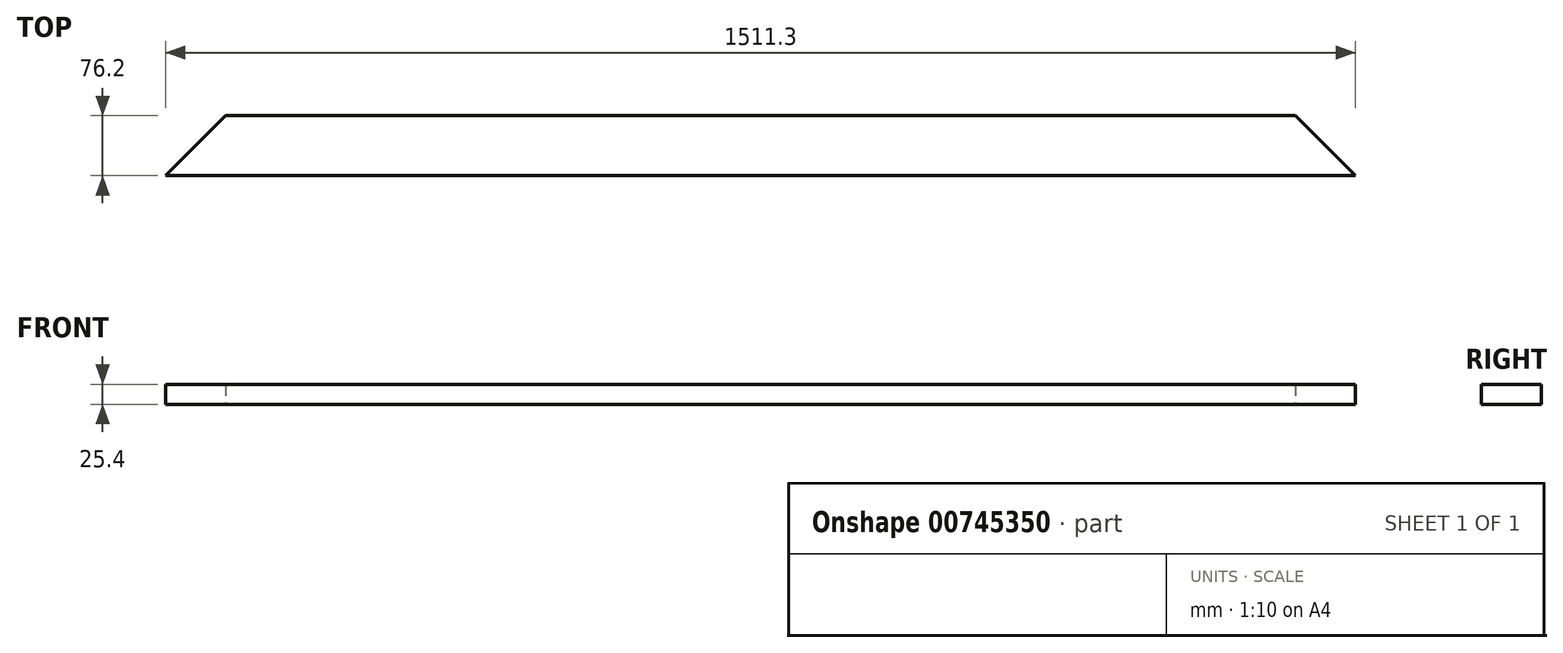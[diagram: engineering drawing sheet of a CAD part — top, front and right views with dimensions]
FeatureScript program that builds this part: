
annotation { "Feature Type Name" : "Feature", "Feature Type Description" : "" }
export const myFeature = defineFeature(function(context is Context, id is Id, definition is map)
    precondition{}
    {
        {
            var Q0;
            Q0=qCreatedBy(makeId("Top.planeOp"),FACE);
            var sketch = newSketch(context, id + "F0", { "sketchPlane" : qUnion([Q0])});
            skLineSegment(sketch, "E0.bottom", {"start": v(0, 0) * mm, "end": v(1511.3, 0) * mm});
            skLineSegment(sketch, "E0.top", {"start": v(76.2, 76.2) * mm, "end": v(1435.1, 76.2) * mm});
            skLineSegment(sketch, "E1", {"start": v(0, 0) * mm, "end": v(76.2, 76.2) * mm});
            skLineSegment(sketch, "E2", {"start": v(1511.3, 0) * mm, "end": v(1435.1, 76.2) * mm});
            skSolve(sketch);
        }
        {
            var Q0;
            Q0=makeQuery(id+"F0.imprint","IMPRINT",FACE,{"disambiguationData":[TD([[makeQuery(id+"F0.imprint","IMPRINT",EDGE,{"derivedFrom":sQuery(id+"F0.wireOp",EDGE,"E0.bottom")}),1.0]])]});
            extrude(context, id + "F1", {"entities" : qUnion([Q0]), "depth" : 25.4 * mm, "offsetDistance" : 25.4 * mm});
        }
    });
